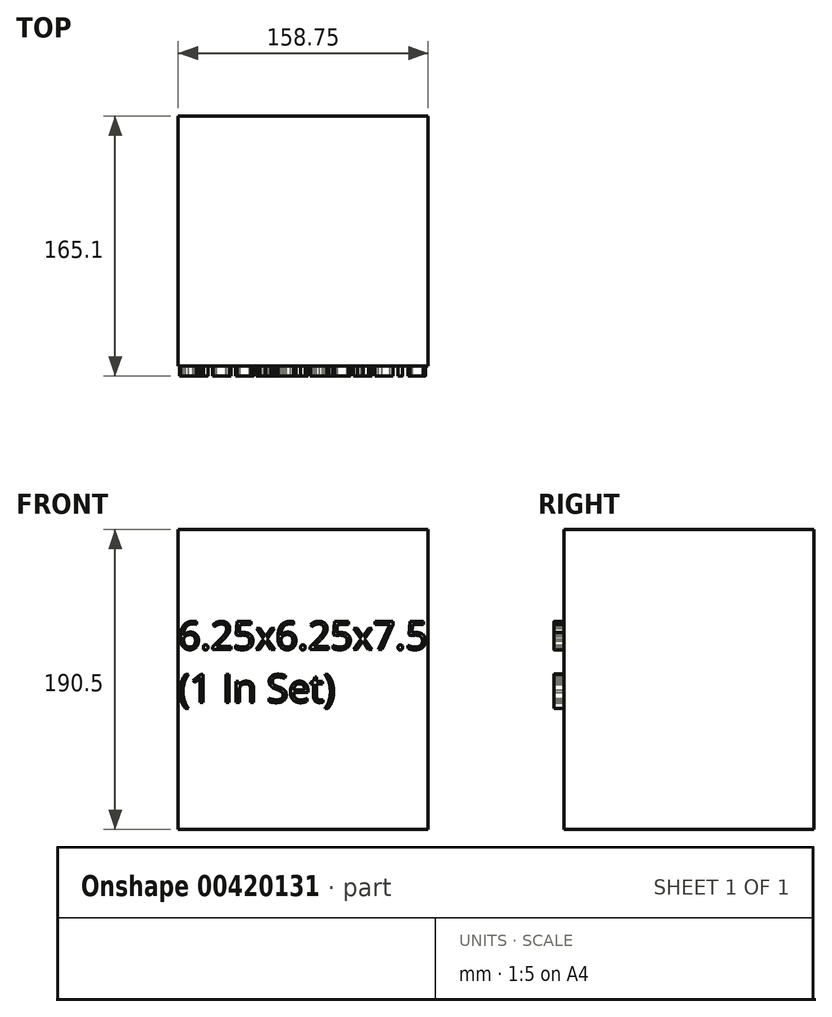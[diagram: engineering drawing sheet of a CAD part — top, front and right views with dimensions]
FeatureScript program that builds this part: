
annotation { "Feature Type Name" : "Feature", "Feature Type Description" : "" }
export const myFeature = defineFeature(function(context is Context, id is Id, definition is map)
    precondition{}
    {
        {
            var Q0;
            Q0=qCreatedBy(makeId("Front.planeOp"),FACE);
            var sketch = newSketch(context, id + "F0", { "sketchPlane" : qUnion([Q0])});
            skLineSegment(sketch, "E0.bottom", {"start": v(0, 0) * mm, "end": v(158.75, 0) * mm});
            skLineSegment(sketch, "E0.top", {"start": v(0, 190.5) * mm, "end": v(158.75, 190.5) * mm});
            skLineSegment(sketch, "E0.left", {"start": v(0, 0) * mm, "end": v(0, 190.5) * mm});
            skLineSegment(sketch, "E0.right", {"start": v(158.75, 0) * mm, "end": v(158.75, 190.5) * mm});
            skSolve(sketch);
        }
        {
            var Q0;
            Q0 = qSketchRegion(id + "F0", true);
            extrude(context, id + "F1", {"entities" : qUnion([Q0]), "depth" : 158.75 * mm});
        }
        {
            var Q0;
            Q0=makeQuery(id+"F1.opExtrude","CAP_FACE",FACE,{"disambiguationData":[OSD([sQuery(id+"F0.wireOp",EDGE,"E0.bottom"),sQuery(id+"F0.wireOp",EDGE,"E0.top"),sQuery(id+"F0.wireOp",EDGE,"E0.left"),sQuery(id+"F0.wireOp",EDGE,"E0.right")])],"isStart":false});
            var sketch = newSketch(context, id + "F2", { "sketchPlane" : qUnion([Q0])});
            skText(sketch, "E1", { "text": "6.25x6.25x7.5\n(1 In Set)", "fontName": "OpenSans-Regular.ttf"});
            const initialGuessF2  = {"E1": [0, 0.11432, 1, 0, 0.01778]};
            skSetInitialGuess(sketch, initialGuessF2);
            skSolve(sketch);
        }
        {
            var Q0;
            Q0 = qSketchRegion(id + "F2", true);
            extrude(context, id + "F3", {"entities" : qUnion([Q0]), "operationType" : NewBodyOperationType.ADD, "depth" : 6.35 * mm});
        }
    });
